# Revit family: Wood_Gear_Designer_Lockers-Salsbury_Industries-30000_Series
name_source: partatom
category: Specialty Equipment
revit_build: Autodesk Revit 2016 (Build: 20150714_1515(x64)
units: mm (PartAtom-declared; Revit-internal decimal feet)

## family parameters
Always vertical = Yes
Cut with Voids When Loaded = No
OmniClass Number = 23.40.00.00
OmniClass Title = Equipment and Furnishings
Part Type = Normal
Room Calculation Point = No
Round Connector Dimension = Use Diameter
Shared = No
Work Plane-Based = No

## types (4) — shared parameters
Assembly Code = C1030310
Door Trim = Rubber Trim - Salsbury Finish - Textured
Hardware = Aluminum - Salsbury Finish - Black Satin
Height = 72.000"
Manufacturer = Salsbury Industries
MasterFormat Code = 10 51 23
MasterFormat Title = Lockers
OmniClass 23 Number = 23.40.00.00
OmniClass 23 Title = Equipment and Furnishings
Primary Structure Materials = Particle Board Industrial Grade - Salsbury Finish - White Melamine Inlay
Secondary Hardware = Steel -Salsbury Finish - Polished Steel
Secondary Structure Materials = Particle Board Industrial Grade - Salsbury Finish - Black Melamine Overlay
Type Comments = 24" Wide Designer Wood Gear Locker
URL = www.lockers.com
Unit Trim = Melamine - Salsbury Finish - Black
Version = 1.0 (10/31/18)
Width = 24.000"

## per-type parameters (varying)
| type | Base | Base Height | Depth | Description | Model | Sloping Hood Height |
| 30074 | Wood Locker Bases : Base - 24" W x 24" D Lockers | 4.000" | 24.750" | 6 Feet High - 24 inches Deep - with Base | 30074 | 0.000" |
| 30078 | Wood Locker Bases : Base - 24" W x 18" D Lockers | 4.000" | 18.750" | 6 Feet High - 18 inches Deep - with Base | 30078 | 0.000" |
| 30074 - without Base | Wood Locker Bases : None | 0.000" | 24.000" | 6 Feet High - 24 inches Deep - without Base | 30074 | 9.118" |
| 30078 - without Base | Wood Locker Bases : None | 0.000" | 18.750" | 6 Feet High - 18 inches Deep - without Base | 30078 | 0.000" |

## geometry (parser evidence)
native form markers: Sweep x18
no freeform markers — native parametric forms only
